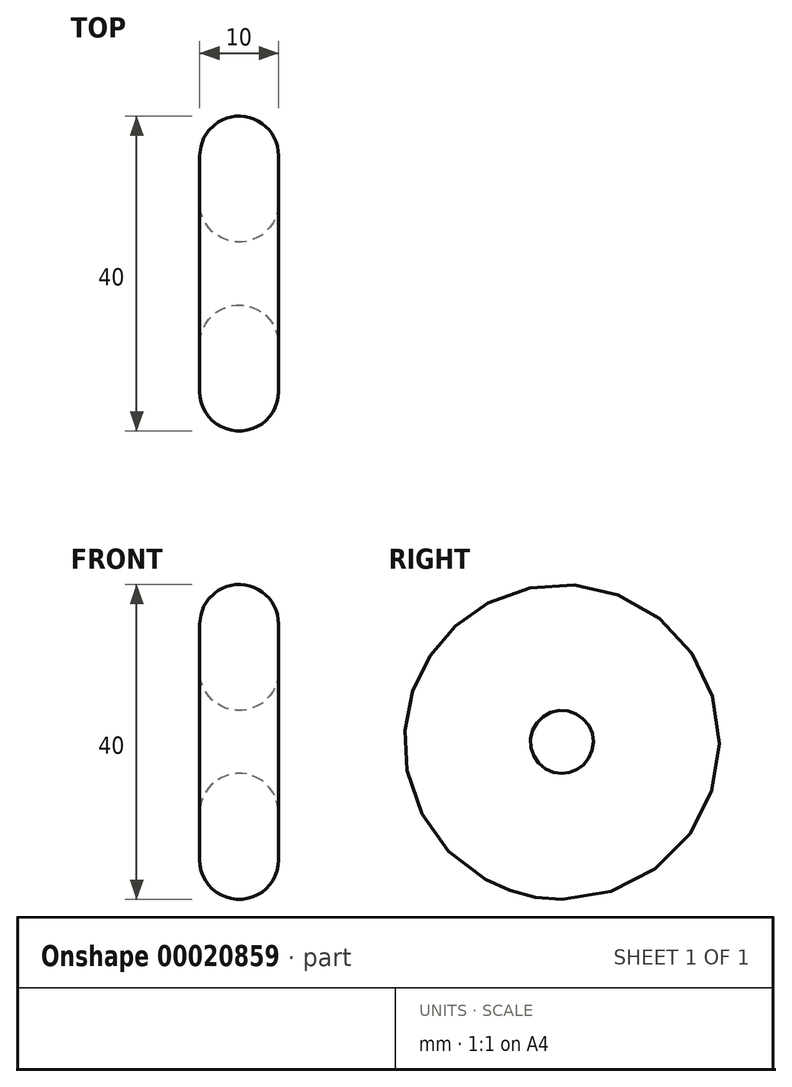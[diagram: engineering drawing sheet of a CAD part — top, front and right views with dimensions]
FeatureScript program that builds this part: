
annotation { "Feature Type Name" : "Feature", "Feature Type Description" : "" }
export const myFeature = defineFeature(function(context is Context, id is Id, definition is map)
    precondition{}
    {
        {
            var Q0;
            Q0=qCreatedBy(makeId("Right.planeOp"),FACE);
            var sketch = newSketch(context, id + "F0", { "sketchPlane" : qUnion([Q0])});
            skCircle(sketch, "E0", {"center": v(0, 0) * mm, "radius": 20 * mm});
            skCircle(sketch, "E1", {"center": v(0, 0) * mm, "radius": 4 * mm});
            skSolve(sketch);
        }
        {
            var Q0;
            Q0=makeQuery(id+"F0.imprint","IMPRINT",FACE,{"disambiguationData":[TD([[makeQuery(id+"F0.imprint","IMPRINT",EDGE,{"derivedFrom":sQuery(id+"F0.wireOp",EDGE,"E0")}),1.0]])]});
            extrude(context, id + "F1", {"entities" : qUnion([Q0]), "depth" : 10 * mm});
        }
        {
            var Q0;
            Q0=makeQuery(id+"F1.opExtrude","CAP_EDGE",EDGE,{"disambiguationData":[OSD([sQuery(id+"F0.wireOp",EDGE,"E0")])],"isStart":false});
            var Q1;
            Q1=makeQuery(id+"F1.opExtrude","CAP_EDGE",EDGE,{"disambiguationData":[OSD([sQuery(id+"F0.wireOp",EDGE,"E1")])],"isStart":false});
            var Q2;
            Q2=makeQuery(id+"F1.opExtrude","CAP_EDGE",EDGE,{"disambiguationData":[OSD([sQuery(id+"F0.wireOp",EDGE,"E0")])],"isStart":true});
            var Q3;
            Q3=makeQuery(id+"F1.opExtrude","CAP_EDGE",EDGE,{"disambiguationData":[OSD([sQuery(id+"F0.wireOp",EDGE,"E1")])],"isStart":true});
            fillet(context, id + "F2", {"entities" : qUnion([Q0, Q1, Q2, Q3]), "radius" : 5 * mm, "tangentPropagation" : true, "allowEdgeOverflow" : false});
        }
    });
